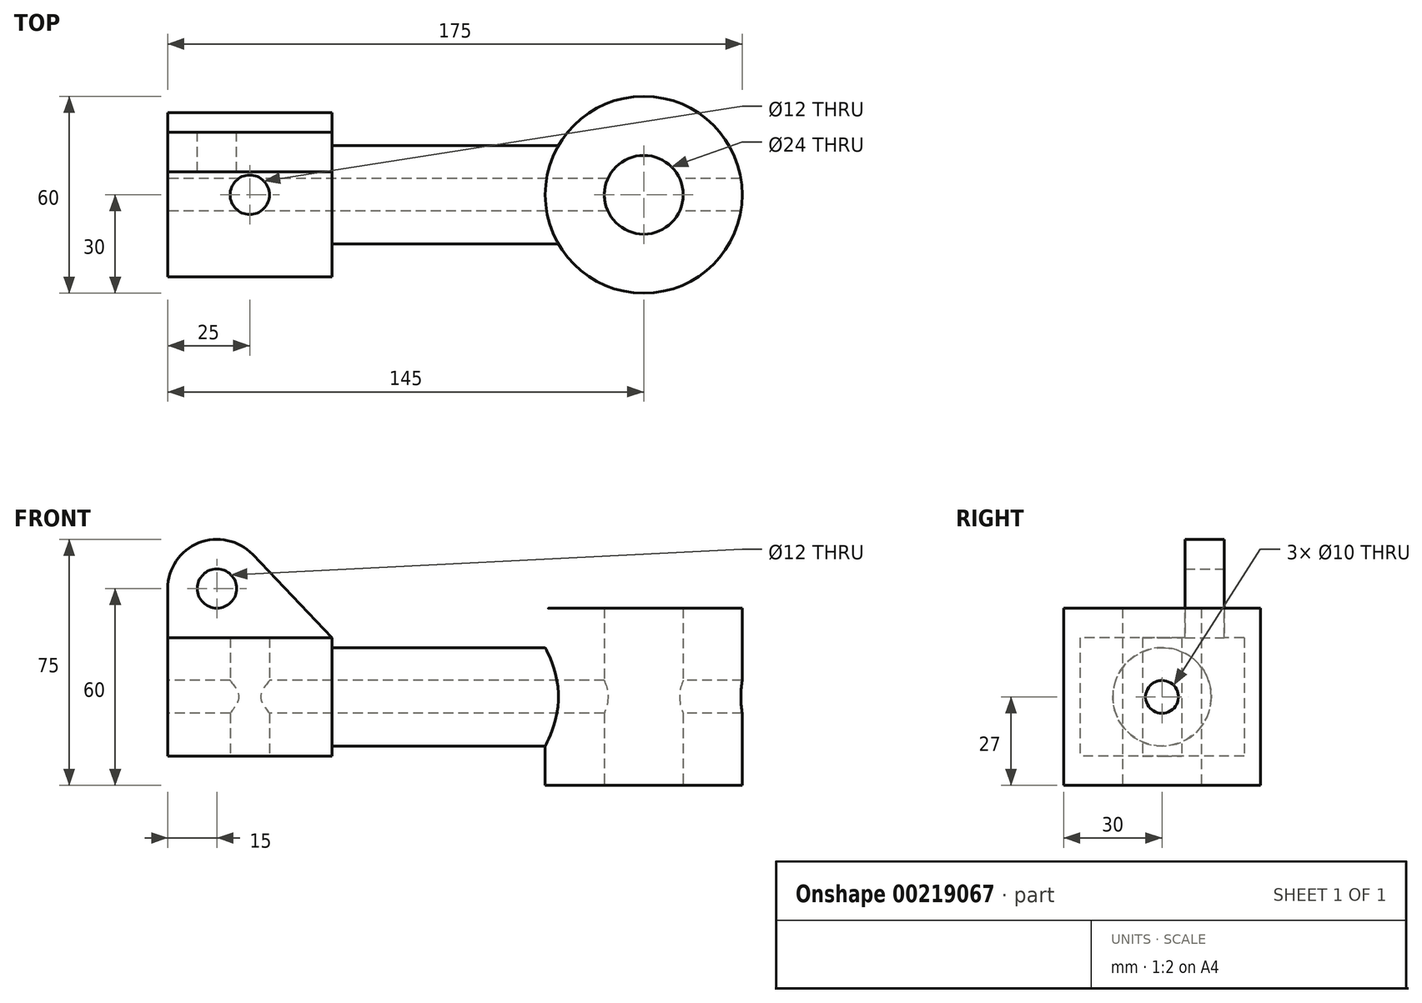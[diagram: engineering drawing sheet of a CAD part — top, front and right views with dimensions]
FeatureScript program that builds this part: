
annotation { "Feature Type Name" : "Feature", "Feature Type Description" : "" }
export const myFeature = defineFeature(function(context is Context, id is Id, definition is map)
    precondition{}
    {
        {
            var Q0;
            Q0=qCreatedBy(makeId("Top.planeOp"),FACE);
            var sketch = newSketch(context, id + "F0", { "sketchPlane" : qUnion([Q0])});
            skLineSegment(sketch, "E0.bottom", {"start": v(25, 25) * mm, "end": v(-25, 25) * mm});
            skLineSegment(sketch, "E0.top", {"start": v(25, -25) * mm, "end": v(-25, -25) * mm});
            skLineSegment(sketch, "E0.left", {"start": v(25, 25) * mm, "end": v(25, -25) * mm});
            skLineSegment(sketch, "E0.right", {"start": v(-25, 25) * mm, "end": v(-25, -25) * mm});
            skPoint(sketch, "E0.middle", {"position": v(0, 0) * mm});
            skLineSegment(sketch, "E1", {"start": v(25, 15) * mm, "end": v(94.02, 15) * mm});
            skCircle(sketch, "E2", {"center": v(120, 0) * mm, "radius": 30 * mm});
            skCircle(sketch, "E3", {"center": v(120, 0) * mm, "radius": 12 * mm});
            skCircle(sketch, "E4", {"center": v(0, 0) * mm, "radius": 6 * mm});
            skLineSegment(sketch, "E5", {"start": v(25, 0) * mm, "end": v(90, 0) * mm});
            skSolve(sketch);
        }
        {
            var Q0;
            {var subQ3=sQuery(id+"F0.wireOp",EDGE,"E0.bottom");Q0=makeQuery(id+"F0.imprint","IMPRINT",FACE,{"disambiguationData":[TD([[makeQuery(id+"F0.imprint","IMPRINT",EDGE,{"derivedFrom":subQ3}),1.0]])]});}
            extrude(context, id + "F1", {"entities" : qUnion([Q0]), "endBound" : BoundingType.SYMMETRIC, "depth" : 36 * mm});
        }
        {
            var Q0;
            {var subQ0=sQuery(id+"F0.wireOp",EDGE,"E1");Q0=makeQuery(id+"F0.imprint","IMPRINT",FACE,{"disambiguationData":[TD([[makeQuery(id+"F0.imprint","IMPRINT",EDGE,{"derivedFrom":subQ0}),-1.0]])]});}
            var Q1;
            Q1=sQuery(id+"F0.wireOp",EDGE,"E5");
            revolve(context, id + "F2", {"operationType" : NewBodyOperationType.ADD, "entities" : qUnion([Q0]), "axis" : qUnion([Q1]), "revolveType" : RevolveType.FULL});
        }
        {
            var Q0;
            Q0=makeQuery(id+"F0.imprint","IMPRINT",FACE,{"disambiguationData":[TD([[makeQuery(id+"F0.imprint","IMPRINT",EDGE,{"derivedFrom":sQuery(id+"F0.wireOp",EDGE,"E3")}),-1.0]])]});
            extrude(context, id + "F3", {"entities" : qUnion([Q0]), "operationType" : NewBodyOperationType.ADD, "endBound" : BoundingType.SYMMETRIC, "depth" : 54 * mm});
        }
        {
            var Q0;
            Q0=makeQuery(id+"F1.opExtrude","SWEPT_FACE",FACE,{"disambiguationData":[OSD([sQuery(id+"F0.wireOp",EDGE,"E0.right")])]});
            var sketch = newSketch(context, id + "F4", { "sketchPlane" : qUnion([Q0])});
            skCircle(sketch, "E6", {"center": v(0, 0) * mm, "radius": 5 * mm});
            skSolve(sketch);
        }
        {
            var Q0;
            Q0 = qSketchRegion(id + "F4", true);
            extrude(context, id + "F5", {"entities" : qUnion([Q0]), "operationType" : NewBodyOperationType.REMOVE, "endBound" : BoundingType.THROUGH_ALL, "oppositeDirection" : true, "depth" : 25 * mm});
        }
        {
            var Q0;
            Q0=makeQuery(id+"F1.opExtrude","SWEPT_FACE",FACE,{"disambiguationData":[OSD([sQuery(id+"F0.wireOp",EDGE,"E0.bottom")])]});
            cPlane(context, id + "F6", {"entities" : qUnion([Q0]), "cplaneType" : CPlaneType.OFFSET, "offset" : 6 * mm, "oppositeDirection" : true, "width" : 150 * mm, "height" : 150 * mm});
        }
        {
            var Q0;
            Q0=qCreatedBy(id+"F6.planeOp",FACE);
            var sketch = newSketch(context, id + "F7", { "sketchPlane" : qUnion([Q0])});
            skCircle(sketch, "E7", {"center": v(10, 33) * mm, "radius": 6 * mm});
            skArc(sketch, "E8", {"start": v(25, 33) * mm, "mid": v(15.57, 46.93) * mm, "end": v(-0.86, 43.34) * mm});
            skPoint(sketch, "E9.0", {"position": v(25, 18) * mm});
            skPoint(sketch, "E10.0", {"position": v(-25, 18) * mm});
            skLineSegment(sketch, "E11", {"start": v(25, 18) * mm, "end": v(25, 33) * mm});
            skLineSegment(sketch, "E12", {"start": v(-0.86, 43.34) * mm, "end": v(-25, 18) * mm});
            skLineSegment(sketch, "E13.0", {"start": v(-25, 18) * mm, "end": v(25, 18) * mm});
            skSolve(sketch);
        }
        {
            var Q0;
            Q0 = qSketchRegion(id + "F7", true);
            extrude(context, id + "F8", {"entities" : qUnion([Q0]), "operationType" : NewBodyOperationType.ADD, "oppositeDirection" : true, "depth" : 12 * mm});
        }
    });
